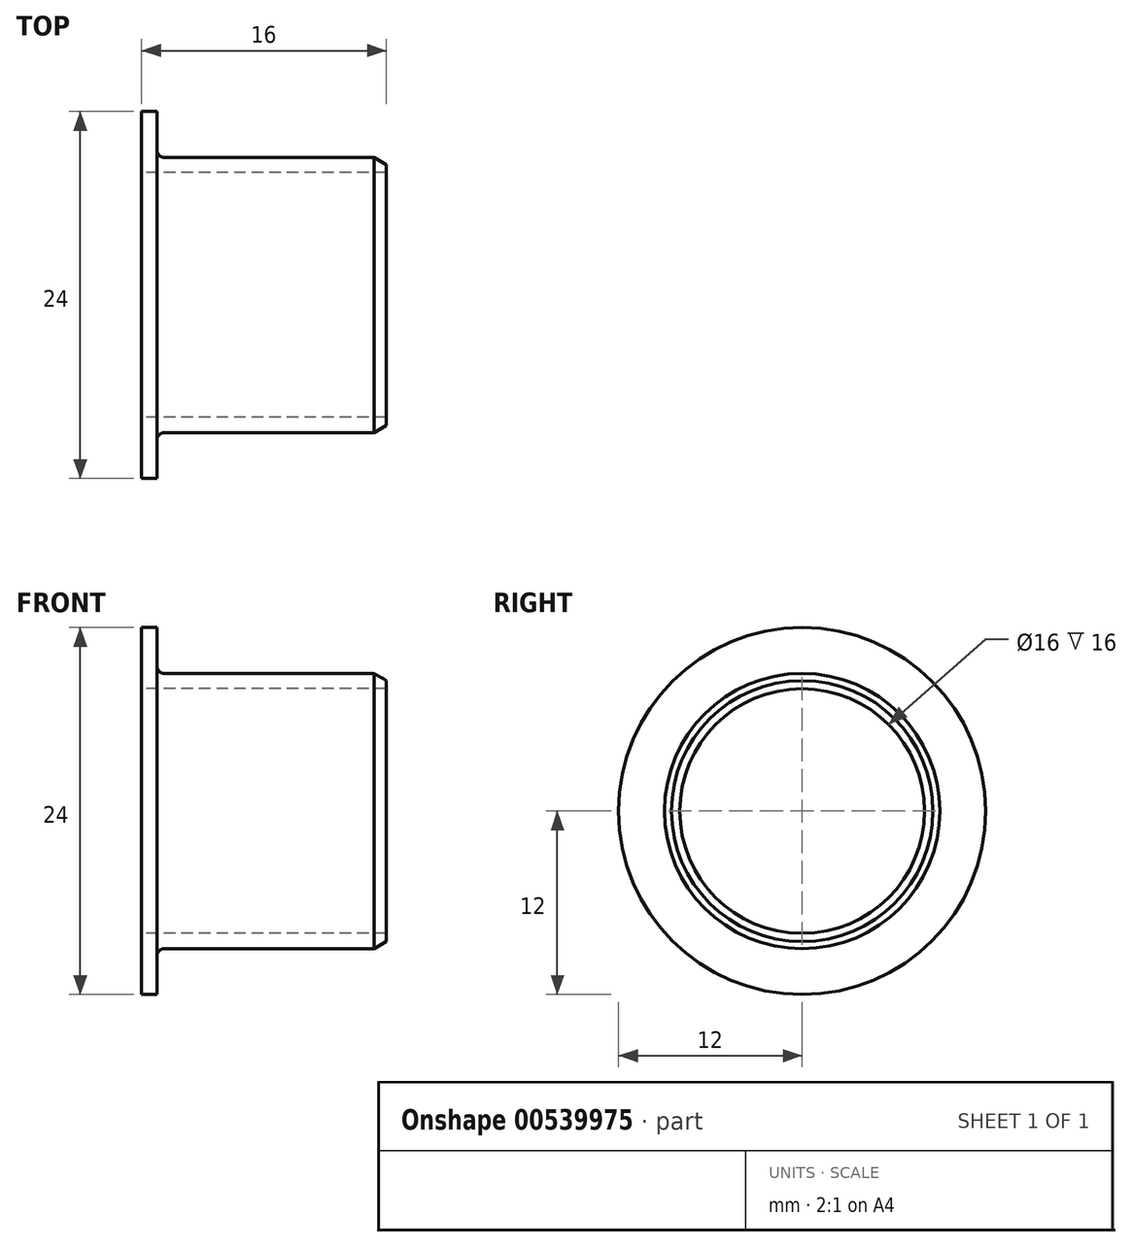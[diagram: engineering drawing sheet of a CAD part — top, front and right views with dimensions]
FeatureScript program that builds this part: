
annotation { "Feature Type Name" : "Feature", "Feature Type Description" : "" }
export const myFeature = defineFeature(function(context is Context, id is Id, definition is map)
    precondition{}
    {
        {
            var Q0;
            Q0=qCreatedBy(makeId("Front.planeOp"),FACE);
            var sketch = newSketch(context, id + "F0", { "sketchPlane" : qUnion([Q0])});
            skLineSegment(sketch, "E0", {"start": v(0, 0) * mm, "end": v(20.85, 0) * mm, "construction": true});
            skLineSegment(sketch, "E1.bottom", {"start": v(0, 0) * mm, "end": v(16, 0) * mm});
            skLineSegment(sketch, "E1.top", {"start": v(0, 8) * mm, "end": v(16, 8) * mm});
            skLineSegment(sketch, "E1.left", {"start": v(0, 0) * mm, "end": v(0, 8) * mm, "construction": true});
            skLineSegment(sketch, "E1.right", {"start": v(16, 0) * mm, "end": v(16, 8) * mm, "construction": true});
            skLineSegment(sketch, "E2.bottom", {"start": v(16, 8) * mm, "end": v(1, 8) * mm});
            skLineSegment(sketch, "E2.top", {"start": v(16, 9) * mm, "end": v(1, 9) * mm});
            skLineSegment(sketch, "E2.left", {"start": v(16, 8) * mm, "end": v(16, 9) * mm});
            skLineSegment(sketch, "E3.bottom", {"start": v(1, 8) * mm, "end": v(0, 8) * mm});
            skLineSegment(sketch, "E3.top", {"start": v(1, 12) * mm, "end": v(0, 12) * mm});
            skLineSegment(sketch, "E3.left", {"start": v(1, 9) * mm, "end": v(1, 12) * mm});
            skLineSegment(sketch, "E3.right", {"start": v(0, 8) * mm, "end": v(0, 12) * mm});
            skSolve(sketch);
        }
        {
            var Q0;
            Q0=makeQuery(id+"F0.imprint","IMPRINT",FACE,{"disambiguationData":[TD([[makeQuery(id+"F0.imprint","IMPRINT",EDGE,{"derivedFrom":sQuery(id+"F0.wireOp",EDGE,"E2.top")}),1.0]])]});
            var Q1;
            Q1=sQuery(id+"F0.wireOp",EDGE,"E1.bottom");
            revolve(context, id + "F1", {"surfaceOperationType" : NewSurfaceOperationType.NEW, "entities" : qUnion([Q0]), "axis" : qUnion([Q1]), "revolveType" : RevolveType.FULL});
        }
        {
            var Q0;
            Q0=makeQuery(id+"F1.opRevolve","SWEPT_EDGE",EDGE,{"disambiguationData":[OSD([sQuery(id+"F0.wireOp",EDGE,"E2.top"),sQuery(id+"F0.wireOp",EDGE,"E2.left")])]});
            chamfer(context, id + "F2", {"entities" : qUnion([Q0]), "chamferType" : ChamferType.OFFSET_ANGLE, "width" : 0.8 * mm, "oppositeDirection" : false, "angle" : 30 * degree, "tangentPropagation" : true});
        }
        {
            var Q0;
            Q0=makeQuery(id+"F1.opRevolve","SWEPT_EDGE",EDGE,{"disambiguationData":[OSD([sQuery(id+"F0.wireOp",EDGE,"E2.top"),sQuery(id+"F0.wireOp",EDGE,"E3.left")])]});
            fillet(context, id + "F3", {"entities" : qUnion([Q0]), "tangentPropagation" : true, "radius" : 0.5 * mm, "defaultsChanged" : true, "vertexSettings" : [], "allowEdgeOverflow" : false});
        }
    });
